# Revit family: Haworth_Pergola_Panel_StraightVerticalTiles
name_source: partatom
category: Furniture Systems
revit_build: Autodesk Revit 2018 (Build: 20170223_1515(x64)
units: mm (PartAtom-declared; Revit-internal decimal feet)

## family parameters
Always vertical = Yes
Cut with Voids When Loaded = No
OmniClass Number = 23.40.70.14.64.21
OmniClass Title = Systems Furniture
Part Type = Normal
Room Calculation Point = No
Round Connector Dimension = Use Diameter
Shared = No
Work Plane-Based = No

## types (8) — shared parameters
Actual Depth = 4 "
Actual Height = 89.5 "
Assembly Code = E2020200
Base Height = 2 "
Bracket Thickness = 0.195 "
Custom Size = No
Description = Haworth - Pergola Panel - Straight - Vertical Tiles
Manufacturer = Haworth
Max. Height = 89.5 "
Max. Width = 144 "
Min. Height = 89.5 "
Min. Width = 48 "
Model = Haworth Pergola
Panel 1 = Yes
Revision Number = 1
Size = Verify Final Dim. w/ Haworth
Standard Width = 48, 72, 96, 120, 144 in.
Sustainability Info = http://www.haworth.com
Trim Finish = Haworth _ Paint _ Undecided _ Pergola
URL = http://www.haworth.com
URL - Product = https://www.haworth.com
Warranty = http://www.haworth.com

## per-type parameters (varying)
| type | Actual Width | Panel 1 - Width | Panel 1 Offset | Panel 2 | Panel 2 - Width | Panel 2 Offset | Panel 3 | Panel 3 - Width | Panel 3 Offset | Panel 4 | Panel 4 - Width | Panel 4 Offset | Width |
| Vertical Tiles - 96h 72w - (36w 36w) | 72 " | 36 " | 18 " | Yes | 36 " | 54 " | No | 0 " | 72 " | No | 0 " | 108 " | 72 " |
| Vertical Tiles - 96h 96w - (48w 48w) | 96 " | 48 " | 24 " | Yes | 48 " | 72 " | No | 0 " | 96 " | No | 0 " | 144 " | 96 " |
| Vertical Tiles - 96h 120w - (48w 36w 36w) | 120 " | 48 " | 24 " | Yes | 36 " | 66 " | Yes | 36 " | 102 " | No | 0 " | 120 " | 120 " |
| Vertical Tiles - 96h 120w - (36w 48w 36w) | 120 " | 36 " | 18 " | Yes | 48 " | 60 " | Yes | 36 " | 102 " | No | 0 " | 132 " | 120 " |
| Vertical Tiles - 96h 120w - (36w 36w 48w) | 120 " | 36 " | 18 " | Yes | 36 " | 54 " | Yes | 48 " | 96 " | No | 0 " | 108 " | 120 " |
| Vertical Tiles - 96h 144w - (48w 48w 48w) | 144 " | 48 " | 24 " | Yes | 48 " | 72 " | Yes | 48 " | 120 " | No | 0 " | 144 " | 144 " |
| Vertical Tiles - 96h 144w - (36w 36w 36w 36w) | 144 " | 36 " | 18 " | Yes | 36 " | 54 " | Yes | 36 " | 90 " | Yes | 36 " | 126 " | 144 " |
| Vertical Tiles - 96h 48w - (48w) | 48 " | 48 " | 24 " | No | 0 " | 48 " | No | 0 " | 48 " | No | 0 " | 48 " | 48 " |

## geometry (parser evidence)
native form markers: Sweep x14
no freeform markers — native parametric forms only
